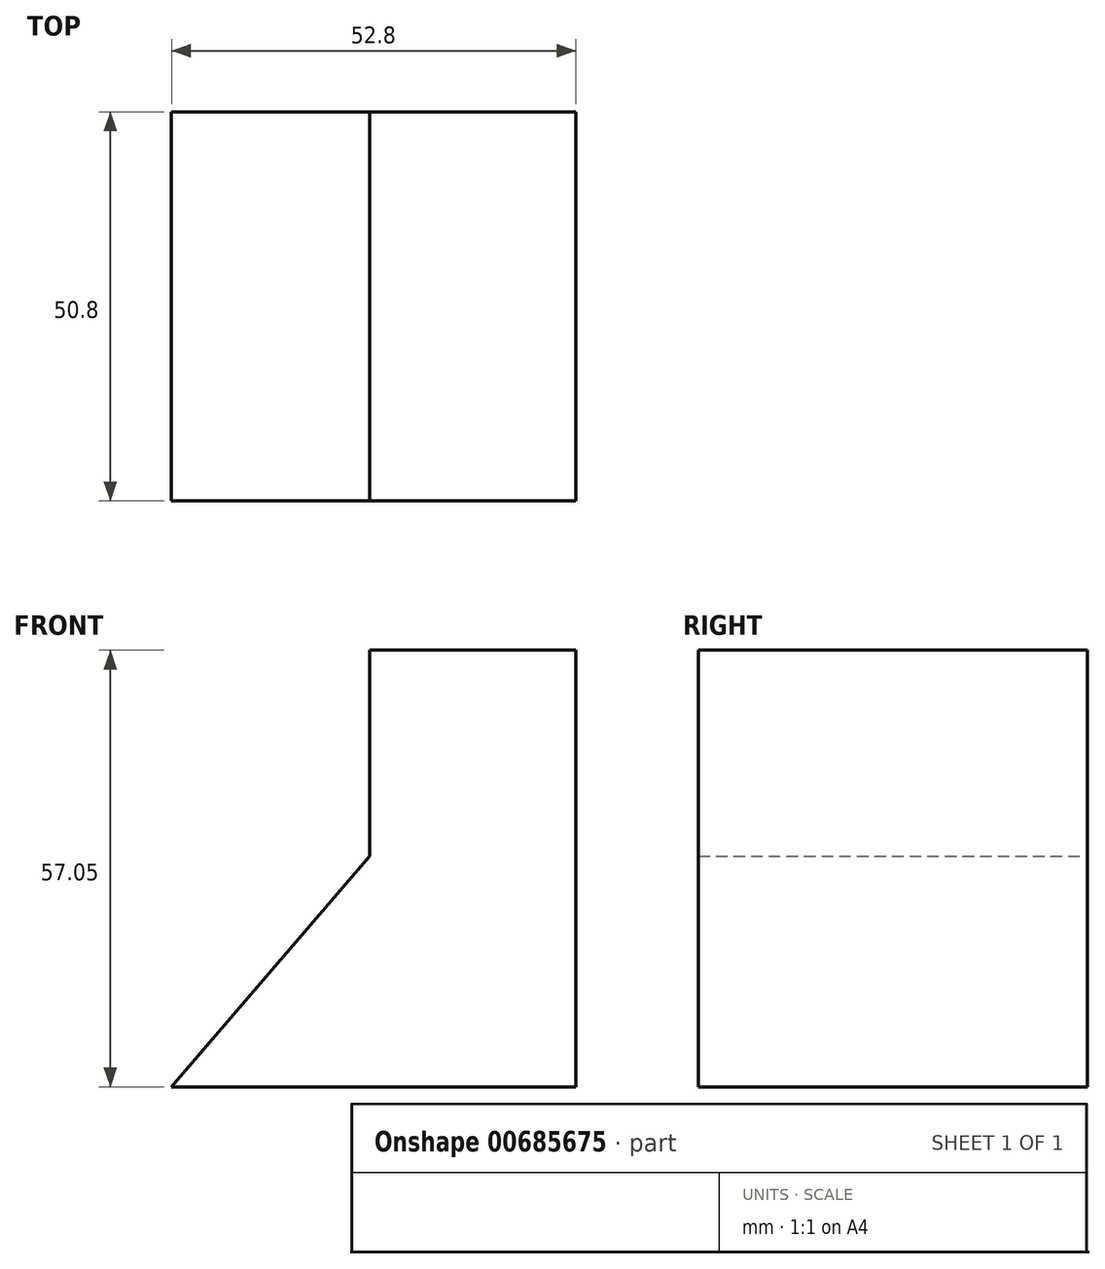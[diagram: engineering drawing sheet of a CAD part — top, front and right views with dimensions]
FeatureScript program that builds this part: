
annotation { "Feature Type Name" : "Feature", "Feature Type Description" : "" }
export const myFeature = defineFeature(function(context is Context, id is Id, definition is map)
    precondition{}
    {
        {
            var Q0;
            Q0=qCreatedBy(makeId("Front.planeOp"),FACE);
            var sketch = newSketch(context, id + "F0", { "sketchPlane" : qUnion([Q0])});
            skLineSegment(sketch, "E0", {"start": v(0, 0) * mm, "end": v(0, 26.9) * mm});
            skLineSegment(sketch, "E1", {"start": v(0, 26.9) * mm, "end": v(26.9, 26.9) * mm});
            skLineSegment(sketch, "E2", {"start": v(26.9, 26.9) * mm, "end": v(26.9, 0) * mm});
            skLineSegment(sketch, "E3", {"start": v(26.9, 0) * mm, "end": v(26.9, -30.14) * mm});
            skLineSegment(sketch, "E4", {"start": v(26.9, -30.14) * mm, "end": v(-25.9, -30.14) * mm});
            skLineSegment(sketch, "E5", {"start": v(-25.9, -30.14) * mm, "end": v(0, 0) * mm});
            skSolve(sketch);
        }
        {
            var Q0;
            Q0=makeQuery(id+"F0.imprint","IMPRINT",FACE,{"disambiguationData":[TD([[makeQuery(id+"F0.imprint","IMPRINT",EDGE,{"derivedFrom":sQuery(id+"F0.wireOp",EDGE,"E0")}),-1.0]])]});
            extrude(context, id + "F1", {"entities" : qUnion([Q0]), "depth" : 50.8 * mm, "offsetDistance" : 25.4 * mm});
        }
    });
